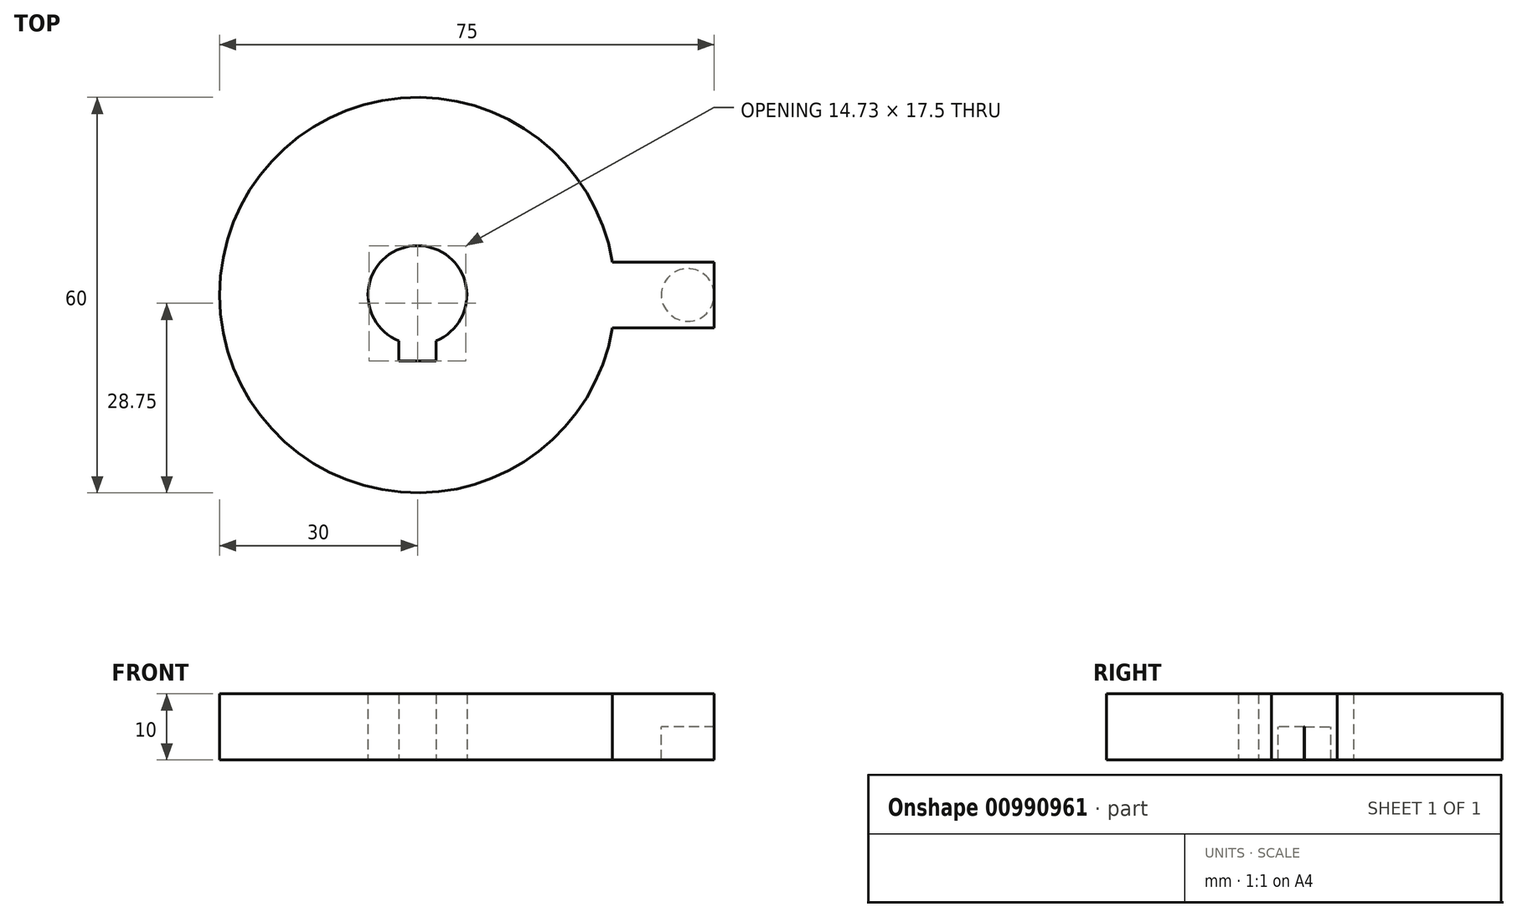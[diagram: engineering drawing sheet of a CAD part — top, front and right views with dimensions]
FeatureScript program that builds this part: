
annotation { "Feature Type Name" : "Feature", "Feature Type Description" : "" }
export const myFeature = defineFeature(function(context is Context, id is Id, definition is map)
    precondition{}
    {
        {
            var Q0;
            Q0=qCreatedBy(makeId("Top.planeOp"),FACE);
            var sketch = newSketch(context, id + "F0", { "sketchPlane" : qUnion([Q0])});
            skCircle(sketch, "E0", {"center": v(0, 0) * mm, "radius": 7.5 * mm});
            skLineSegment(sketch, "E1", {"start": v(0, 0) * mm, "end": v(0, -10) * mm, "construction": true});
            skLineSegment(sketch, "E2", {"start": v(0, -10) * mm, "end": v(-2.8, -10) * mm});
            skLineSegment(sketch, "E3", {"start": v(-2.8, -10) * mm, "end": v(-2.8, -6.96) * mm});
            skCircle(sketch, "E4", {"center": v(0, 0) * mm, "radius": 30 * mm});
            skLineSegment(sketch, "E5.MirrorCS", {"start": v(0, -10) * mm, "end": v(2.8, -10) * mm});
            skLineSegment(sketch, "E6.MirrorCS", {"start": v(2.8, -10) * mm, "end": v(2.8, -6.96) * mm});
            skPoint(sketch, "E7", {"position": v(0, -7.5) * mm});
            skLineSegment(sketch, "E8", {"start": v(0, 0) * mm, "end": v(71.76, 0) * mm, "construction": true});
            skLineSegment(sketch, "E9", {"start": v(45, 0) * mm, "end": v(45, -5) * mm});
            skLineSegment(sketch, "E10", {"start": v(45, -5) * mm, "end": v(29.58, -5) * mm});
            skPoint(sketch, "E11", {"position": v(30, 0) * mm});
            skLineSegment(sketch, "E12.MirrorCS", {"start": v(45, 5) * mm, "end": v(29.58, 5) * mm});
            skLineSegment(sketch, "E13.MirrorCS", {"start": v(45, 0) * mm, "end": v(45, 5) * mm});
            skSolve(sketch);
        }
        {
            var Q0;
            Q0 = qSketchRegion(id + "F0", true);
            extrude(context, id + "F1", {"entities" : qUnion([Q0]), "endBound" : BoundingType.SYMMETRIC, "depth" : 5 * mm, "offsetDistance" : 25 * mm});
        }
        {
            var Q0;
            Q0=makeQuery(id+"F1.opExtrude","CAP_FACE",FACE,{"disambiguationData":[OSD([sQuery(id+"F0.wireOp",EDGE,"E0"),sQuery(id+"F0.wireOp",EDGE,"E2"),sQuery(id+"F0.wireOp",EDGE,"E3"),sQuery(id+"F0.wireOp",EDGE,"E4"),sQuery(id+"F0.wireOp",EDGE,"E5.MirrorCS"),sQuery(id+"F0.wireOp",EDGE,"E6.MirrorCS"),sQuery(id+"F0.wireOp",EDGE,"E9"),sQuery(id+"F0.wireOp",EDGE,"E10"),sQuery(id+"F0.wireOp",EDGE,"E12.MirrorCS"),sQuery(id+"F0.wireOp",EDGE,"E13.MirrorCS")])],"isStart":true});
            var sketch = newSketch(context, id + "F2", { "sketchPlane" : qUnion([Q0])});
            skCircle(sketch, "E14", {"center": v(41, -0.02) * mm, "radius": 4 * mm});
            skPoint(sketch, "E14.first.point", {"position": v(45, 0) * mm});
            skPoint(sketch, "E14.second.point", {"position": v(37, 0) * mm});
            skPoint(sketch, "E14.second.point.positionSnap0", {"position": v(45, 0) * mm});
            skPoint(sketch, "E14.third.point", {"position": v(38.86, 3.36) * mm});
            skSolve(sketch);
        }
        {
            var Q0;
            {var subQ0=sQuery(id+"F2.wireOp",EDGE,"E14");Q0=makeQuery(id+"F2.imprint","IMPRINT",FACE,{"disambiguationData":[TD([[makeQuery(id+"F2.imprint","IMPRINT",EDGE,{"disambiguationData":[OD(0.0)],"derivedFrom":subQ0}),-1.0]])]});}
            extrude(context, id + "F3", {"entities" : qUnion([Q0]), "operationType" : NewBodyOperationType.ADD, "depth" : 5 * mm, "offsetDistance" : 25 * mm});
        }
    });
